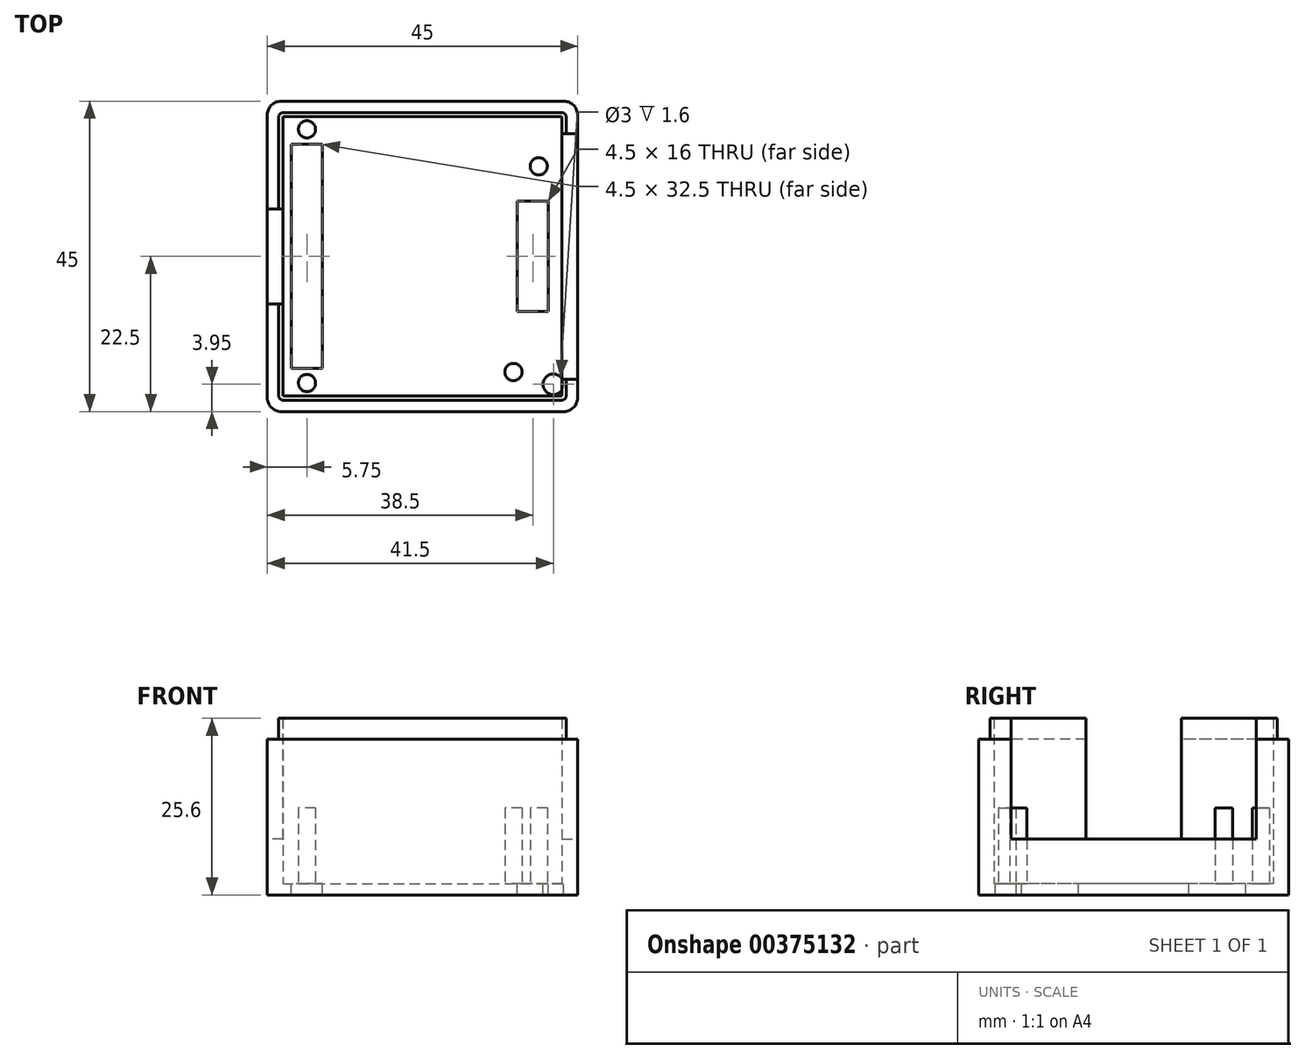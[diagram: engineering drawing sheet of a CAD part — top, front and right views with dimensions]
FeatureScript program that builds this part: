
annotation { "Feature Type Name" : "Feature", "Feature Type Description" : "" }
export const myFeature = defineFeature(function(context is Context, id is Id, definition is map)
    precondition{}
    {
        {
            var Q0;
            Q0=qCreatedBy(makeId("Top.planeOp"),FACE);
            var sketch = newSketch(context, id + "F0", { "sketchPlane" : qUnion([Q0])});
            skLineSegment(sketch, "E0.bottom", {"start": v(-20.5, 22.5) * mm, "end": v(20.5, 22.5) * mm});
            skLineSegment(sketch, "E0.top", {"start": v(-20.5, -22.5) * mm, "end": v(20.5, -22.5) * mm});
            skLineSegment(sketch, "E0.left", {"start": v(-22.5, 20.5) * mm, "end": v(-22.5, -20.5) * mm});
            skLineSegment(sketch, "E0.right", {"start": v(22.5, 20.5) * mm, "end": v(22.5, -20.5) * mm});
            skPoint(sketch, "E1.visualSharp", {"position": v(-22.5, 22.5) * mm});
            skArc(sketch, "E1.filletArc", {"start": v(-20.5, 22.5) * mm, "mid": v(-21.91, 21.91) * mm, "end": v(-22.5, 20.5) * mm});
            skPoint(sketch, "E2.visualSharp", {"position": v(22.5, 22.5) * mm});
            skArc(sketch, "E2.filletArc", {"start": v(22.5, 20.5) * mm, "mid": v(21.91, 21.91) * mm, "end": v(20.5, 22.5) * mm});
            skPoint(sketch, "E3.visualSharp", {"position": v(-22.5, -22.5) * mm});
            skArc(sketch, "E3.filletArc", {"start": v(-22.5, -20.5) * mm, "mid": v(-21.91, -21.91) * mm, "end": v(-20.5, -22.5) * mm});
            skPoint(sketch, "E4.visualSharp", {"position": v(22.5, -22.5) * mm});
            skArc(sketch, "E4.filletArc", {"start": v(20.5, -22.5) * mm, "mid": v(21.91, -21.91) * mm, "end": v(22.5, -20.5) * mm});
            skLineSegment(sketch, "E5.bottom", {"start": v(-20.25, 20.25) * mm, "end": v(20.25, 20.25) * mm});
            skLineSegment(sketch, "E5.top", {"start": v(-20.25, -20.25) * mm, "end": v(20.25, -20.25) * mm});
            skLineSegment(sketch, "E5.left", {"start": v(-20.25, 20.25) * mm, "end": v(-20.25, -20.25) * mm});
            skLineSegment(sketch, "E5.right", {"start": v(20.25, 20.25) * mm, "end": v(20.25, -20.25) * mm});
            skSolve(sketch);
        }
        {
            var Q0;
            Q0=makeQuery(id+"F0.imprint","IMPRINT",FACE,{"disambiguationData":[TD([[makeQuery(id+"F0.imprint","IMPRINT",EDGE,{"derivedFrom":sQuery(id+"F0.wireOp",EDGE,"E5.bottom")}),-1.0]])]});
            extrude(context, id + "F1", {"entities" : qUnion([Q0]), "depth" : 1.6 * mm});
        }
        {
            var Q0;
            Q0=qSketchRegion(id+"F0",true);
            extrude(context, id + "F2", {"entities" : qUnion([Q0]), "operationType" : NewBodyOperationType.ADD, "depth" : 22.6 * mm});
        }
        {
            var Q0;
            Q0=makeQuery(id+"F2.opExtrude","CAP_FACE",FACE,{"disambiguationData":[OSD([sQuery(id+"F0.wireOp",EDGE,"E0.bottom"),sQuery(id+"F0.wireOp",EDGE,"E0.top"),sQuery(id+"F0.wireOp",EDGE,"E0.left"),sQuery(id+"F0.wireOp",EDGE,"E0.right"),sQuery(id+"F0.wireOp",EDGE,"E1.filletArc"),sQuery(id+"F0.wireOp",EDGE,"E2.filletArc"),sQuery(id+"F0.wireOp",EDGE,"E3.filletArc"),sQuery(id+"F0.wireOp",EDGE,"E4.filletArc"),sQuery(id+"F0.wireOp",EDGE,"E5.bottom"),sQuery(id+"F0.wireOp",EDGE,"E5.top"),sQuery(id+"F0.wireOp",EDGE,"E5.left"),sQuery(id+"F0.wireOp",EDGE,"E5.right")])],"isStart":false});
            var sketch = newSketch(context, id + "F3", { "sketchPlane" : qUnion([Q0])});
            skLineSegment(sketch, "E6.bottom", {"start": v(-20.25, 20.25) * mm, "end": v(20.25, 20.25) * mm});
            skLineSegment(sketch, "E6.top", {"start": v(-20.25, -20.25) * mm, "end": v(20.25, -20.25) * mm});
            skLineSegment(sketch, "E6.left", {"start": v(-20.25, 20.25) * mm, "end": v(-20.25, -20.25) * mm});
            skLineSegment(sketch, "E6.right", {"start": v(20.25, 20.25) * mm, "end": v(20.25, -20.25) * mm});
            skLineSegment(sketch, "E7.0", {"start": v(-20.2, 20.85) * mm, "end": v(20.2, 20.85) * mm});
            skLineSegment(sketch, "E7.1", {"start": v(-20.85, 20.2) * mm, "end": v(-20.85, -20.2) * mm});
            skLineSegment(sketch, "E7.2", {"start": v(-20.2, -20.85) * mm, "end": v(20.2, -20.85) * mm});
            skLineSegment(sketch, "E7.3", {"start": v(20.85, 20.2) * mm, "end": v(20.85, -20.2) * mm});
            skPoint(sketch, "E8.visualSharp", {"position": v(-20.85, 20.85) * mm});
            skArc(sketch, "E8.filletArc", {"start": v(-20.2, 20.85) * mm, "mid": v(-20.66, 20.66) * mm, "end": v(-20.85, 20.2) * mm});
            skPoint(sketch, "E9.visualSharp", {"position": v(20.85, 20.85) * mm});
            skArc(sketch, "E9.filletArc", {"start": v(20.85, 20.2) * mm, "mid": v(20.66, 20.66) * mm, "end": v(20.2, 20.85) * mm});
            skPoint(sketch, "E10.visualSharp", {"position": v(20.85, -20.85) * mm});
            skArc(sketch, "E10.filletArc", {"start": v(20.2, -20.85) * mm, "mid": v(20.66, -20.66) * mm, "end": v(20.85, -20.2) * mm});
            skPoint(sketch, "E11.visualSharp", {"position": v(-20.85, -20.85) * mm});
            skArc(sketch, "E11.filletArc", {"start": v(-20.85, -20.2) * mm, "mid": v(-20.66, -20.66) * mm, "end": v(-20.2, -20.85) * mm});
            skSolve(sketch);
        }
        {
            var Q0;
            Q0=makeQuery(id+"F3.imprint","IMPRINT",FACE,{"disambiguationData":[TD([[makeQuery(id+"F3.imprint","IMPRINT",EDGE,{"derivedFrom":sQuery(id+"F3.wireOp",EDGE,"E6.bottom")}),1.0]])]});
            extrude(context, id + "F4", {"entities" : qUnion([Q0]), "operationType" : NewBodyOperationType.ADD, "depth" : 3 * mm});
        }
        {
            var Q0;
            Q0=makeQuery(id+"F2.opExtrude","SWEPT_FACE",FACE,{"disambiguationData":[OSD([sQuery(id+"F0.wireOp",EDGE,"E0.right")])]});
            var sketch = newSketch(context, id + "F5", { "sketchPlane" : qUnion([Q0])});
            skLineSegment(sketch, "E12.bottom", {"start": v(-17.8, 25.6) * mm, "end": v(17.8, 25.6) * mm});
            skLineSegment(sketch, "E12.top", {"start": v(-17.8, 8.1) * mm, "end": v(17.8, 8.1) * mm});
            skLineSegment(sketch, "E12.left", {"start": v(-17.8, 25.6) * mm, "end": v(-17.8, 8.1) * mm});
            skLineSegment(sketch, "E12.right", {"start": v(17.8, 25.6) * mm, "end": v(17.8, 8.1) * mm});
            skSolve(sketch);
        }
        {
            var Q0;
            {var subQ0=sQuery(id+"F5.wireOp",EDGE,"E12.top");Q0=makeQuery(id+"F5.imprint","IMPRINT",FACE,{"disambiguationData":[TD([[makeQuery(id+"F5.imprint","IMPRINT",EDGE,{"derivedFrom":subQ0}),1.0]])]});}
            var Q1;
            {var subQ0=sQuery(id+"F5.wireOp",EDGE,"E12.bottom");Q1=makeQuery(id+"F5.imprint","IMPRINT",FACE,{"disambiguationData":[TD([[makeQuery(id+"F5.imprint","IMPRINT",EDGE,{"derivedFrom":subQ0}),-1.0]])]});}
            extrude(context, id + "F6", {"entities" : qUnion([Q0, Q1]), "operationType" : NewBodyOperationType.REMOVE, "oppositeDirection" : true, "depth" : 5 * mm});
        }
        {
            var Q0;
            Q0=makeQuery(id+"F2.opExtrude","SWEPT_FACE",FACE,{"disambiguationData":[OSD([sQuery(id+"F0.wireOp",EDGE,"E0.left")])]});
            var sketch = newSketch(context, id + "F7", { "sketchPlane" : qUnion([Q0])});
            skLineSegment(sketch, "E13.bottom", {"start": v(-6.9, 25.6) * mm, "end": v(6.9, 25.6) * mm});
            skLineSegment(sketch, "E13.top", {"start": v(-6.9, 8.1) * mm, "end": v(6.9, 8.1) * mm});
            skLineSegment(sketch, "E13.left", {"start": v(-6.9, 25.6) * mm, "end": v(-6.9, 8.1) * mm});
            skLineSegment(sketch, "E13.right", {"start": v(6.9, 25.6) * mm, "end": v(6.9, 8.1) * mm});
            skSolve(sketch);
        }
        {
            var Q0;
            {var subQ0=sQuery(id+"F7.wireOp",EDGE,"E13.top");Q0=makeQuery(id+"F7.imprint","IMPRINT",FACE,{"disambiguationData":[TD([[makeQuery(id+"F7.imprint","IMPRINT",EDGE,{"derivedFrom":subQ0}),1.0]])]});}
            var Q1;
            {var subQ0=sQuery(id+"F7.wireOp",EDGE,"E13.bottom");Q1=makeQuery(id+"F7.imprint","IMPRINT",FACE,{"disambiguationData":[TD([[makeQuery(id+"F7.imprint","IMPRINT",EDGE,{"derivedFrom":subQ0}),-1.0]])]});}
            extrude(context, id + "F8", {"entities" : qUnion([Q0, Q1]), "operationType" : NewBodyOperationType.REMOVE, "oppositeDirection" : true, "depth" : 5 * mm});
        }
        {
            var Q0;
            Q0=makeQuery(id+"F1.opExtrude","CAP_FACE",FACE,{"disambiguationData":[OSD([sQuery(id+"F0.wireOp",EDGE,"E5.bottom"),sQuery(id+"F0.wireOp",EDGE,"E5.top"),sQuery(id+"F0.wireOp",EDGE,"E5.left"),sQuery(id+"F0.wireOp",EDGE,"E5.right")])],"isStart":false});
            var sketch = newSketch(context, id + "F9", { "sketchPlane" : qUnion([Q0])});
            skLineSegment(sketch, "E14.bottom", {"start": v(18.25, 8) * mm, "end": v(13.75, 8) * mm});
            skLineSegment(sketch, "E14.top", {"start": v(18.25, -8) * mm, "end": v(13.75, -8) * mm});
            skLineSegment(sketch, "E14.left", {"start": v(18.25, 8) * mm, "end": v(18.25, -8) * mm});
            skLineSegment(sketch, "E14.right", {"start": v(13.75, 8) * mm, "end": v(13.75, -8) * mm});
            skLineSegment(sketch, "E15.bottom", {"start": v(-14.5, 16.25) * mm, "end": v(-19, 16.25) * mm});
            skLineSegment(sketch, "E15.top", {"start": v(-14.5, -16.25) * mm, "end": v(-19, -16.25) * mm});
            skLineSegment(sketch, "E15.left", {"start": v(-14.5, 16.25) * mm, "end": v(-14.5, -16.25) * mm});
            skLineSegment(sketch, "E15.right", {"start": v(-19, 16.25) * mm, "end": v(-19, -16.25) * mm});
            skCircle(sketch, "E16", {"center": v(19, -18.55) * mm, "radius": 1.5 * mm});
            skSolve(sketch);
        }
        {
            var Q0;
            Q0=makeQuery(id+"F9.imprint","IMPRINT",FACE,{"disambiguationData":[TD([[makeQuery(id+"F9.imprint","IMPRINT",EDGE,{"derivedFrom":sQuery(id+"F9.wireOp",EDGE,"E14.bottom")}),1.0]])]});
            var Q1;
            Q1=makeQuery(id+"F9.imprint","IMPRINT",FACE,{"disambiguationData":[TD([[makeQuery(id+"F9.imprint","IMPRINT",EDGE,{"derivedFrom":sQuery(id+"F9.wireOp",EDGE,"E16")}),1.0]])]});
            var Q2;
            Q2=makeQuery(id+"F9.imprint","IMPRINT",FACE,{"disambiguationData":[TD([[makeQuery(id+"F9.imprint","IMPRINT",EDGE,{"derivedFrom":sQuery(id+"F9.wireOp",EDGE,"E15.bottom")}),1.0]])]});
            extrude(context, id + "F10", {"entities" : qUnion([Q0, Q1, Q2]), "operationType" : NewBodyOperationType.REMOVE, "oppositeDirection" : true, "depth" : 5 * mm});
        }
        {
            var Q0;
            Q0=makeQuery(id+"F1.opExtrude","CAP_FACE",FACE,{"disambiguationData":[OSD([sQuery(id+"F0.wireOp",EDGE,"E5.bottom"),sQuery(id+"F0.wireOp",EDGE,"E5.top"),sQuery(id+"F0.wireOp",EDGE,"E5.left"),sQuery(id+"F0.wireOp",EDGE,"E5.right")])],"isStart":false});
            var sketch = newSketch(context, id + "F11", { "sketchPlane" : qUnion([Q0])});
            skCircle(sketch, "E17", {"center": v(16.87, 13.07) * mm, "radius": 1.25 * mm});
            skCircle(sketch, "E18", {"center": v(-16.75, 18.43) * mm, "radius": 1.25 * mm});
            skPoint(sketch, "E18.centerSnap0", {"position": v(-16.75, 16.25) * mm});
            skCircle(sketch, "E19", {"center": v(-16.75, -18.35) * mm, "radius": 1.25 * mm});
            skPoint(sketch, "E19.centerSnap0", {"position": v(-16.75, -16.25) * mm});
            skCircle(sketch, "E20", {"center": v(13.2, -16.76) * mm, "radius": 1.25 * mm});
            skSolve(sketch);
        }
        {
            var Q0;
            Q0=makeQuery(id+"F11.imprint","IMPRINT",FACE,{"disambiguationData":[TD([[makeQuery(id+"F11.imprint","IMPRINT",EDGE,{"derivedFrom":sQuery(id+"F11.wireOp",EDGE,"E17")}),1.0]])]});
            var Q1;
            Q1=makeQuery(id+"F11.imprint","IMPRINT",FACE,{"disambiguationData":[TD([[makeQuery(id+"F11.imprint","IMPRINT",EDGE,{"derivedFrom":sQuery(id+"F11.wireOp",EDGE,"E18")}),1.0]])]});
            var Q2;
            Q2=makeQuery(id+"F11.imprint","IMPRINT",FACE,{"disambiguationData":[TD([[makeQuery(id+"F11.imprint","IMPRINT",EDGE,{"derivedFrom":sQuery(id+"F11.wireOp",EDGE,"E19")}),1.0]])]});
            var Q3;
            Q3=makeQuery(id+"F11.imprint","IMPRINT",FACE,{"disambiguationData":[TD([[makeQuery(id+"F11.imprint","IMPRINT",EDGE,{"derivedFrom":sQuery(id+"F11.wireOp",EDGE,"E20")}),1.0]])]});
            extrude(context, id + "F12", {"entities" : qUnion([Q0, Q1, Q2, Q3]), "operationType" : NewBodyOperationType.ADD, "depth" : 11 * mm});
        }
    });
